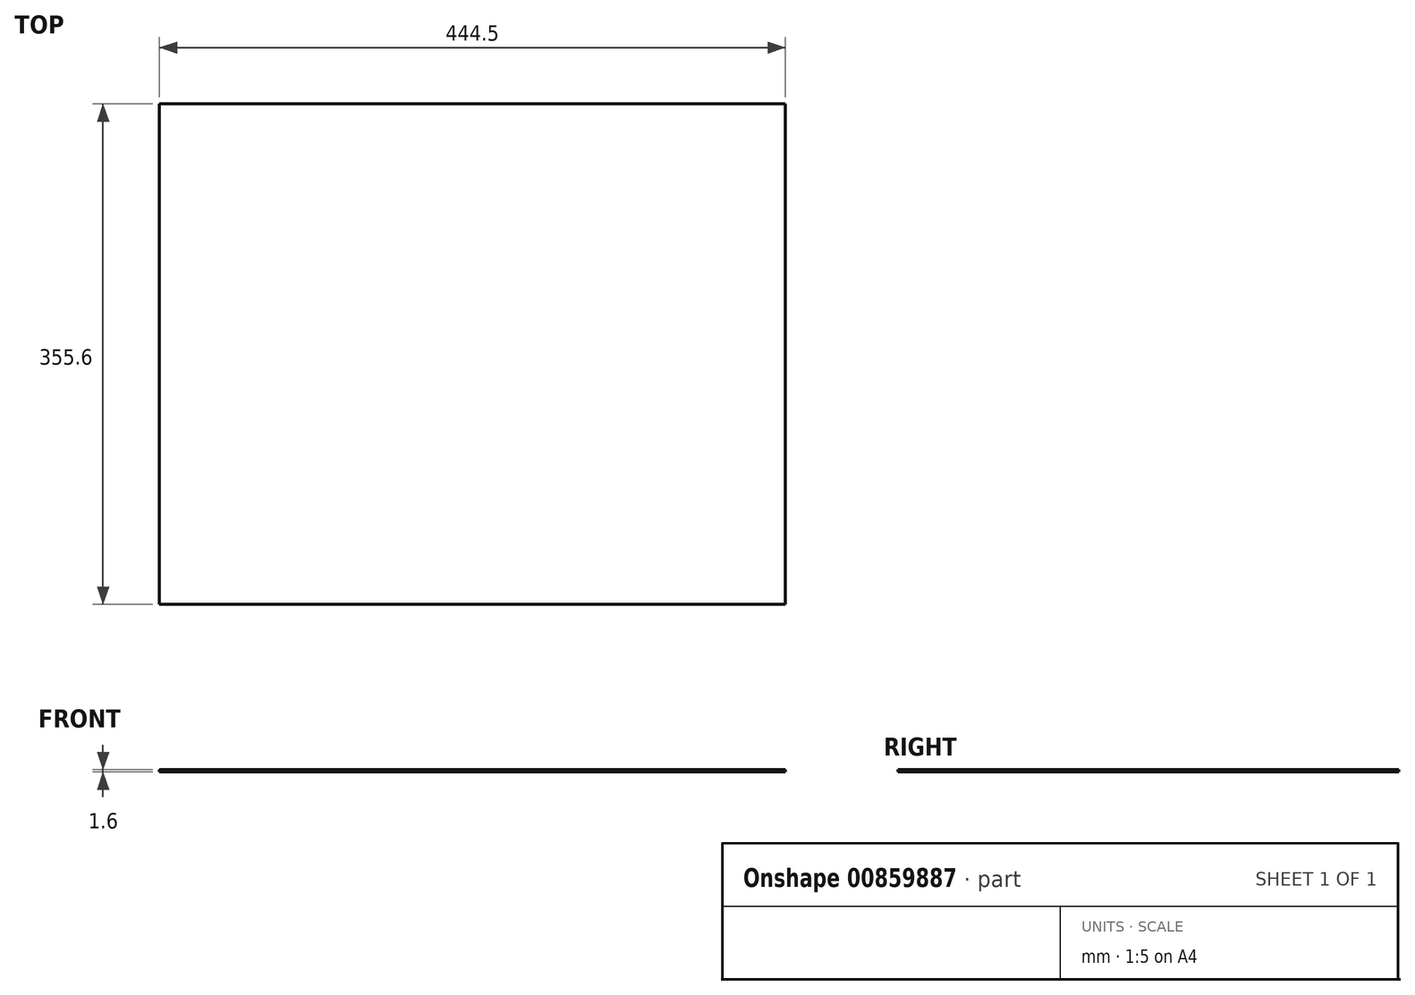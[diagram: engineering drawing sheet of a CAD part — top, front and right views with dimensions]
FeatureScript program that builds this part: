
annotation { "Feature Type Name" : "Feature", "Feature Type Description" : "" }
export const myFeature = defineFeature(function(context is Context, id is Id, definition is map)
    precondition{}
    {
        {
            assignVariable(context, id + "F0", {"name" : "ServerHeight", "anyValue" : 1.6});
        }
        {
            var Q0;
            Q0=qCreatedBy(makeId("Top.planeOp"),FACE);
            var sketch = newSketch(context, id + "F1", { "sketchPlane" : qUnion([Q0])});
            skLineSegment(sketch, "E0.bottom", {"start": v(222.25, -177.8) * mm, "end": v(-222.25, -177.8) * mm});
            skLineSegment(sketch, "E0.top", {"start": v(222.25, 177.8) * mm, "end": v(-222.25, 177.8) * mm});
            skLineSegment(sketch, "E0.left", {"start": v(222.25, -177.8) * mm, "end": v(222.25, 177.8) * mm});
            skLineSegment(sketch, "E0.right", {"start": v(-222.25, -177.8) * mm, "end": v(-222.25, 177.8) * mm});
            skPoint(sketch, "E0.middle", {"position": v(0, 0) * mm});
            skSolve(sketch);
        }
        {
            var Q0;
            Q0=makeQuery(id+"F1.imprint","IMPRINT",FACE,{"disambiguationData":[TD([[makeQuery(id+"F1.imprint","IMPRINT",EDGE,{"derivedFrom":sQuery(id+"F1.wireOp",EDGE,"E0.bottom")}),-1.0]])]});
            extrude(context, id + "F2", {"entities" : qUnion([Q0]), "depth" : (getVariable(context, 'ServerHeight')) * mm, "offsetDistance" : 25.4 * mm});
        }
        {
            var Q0;
            Q0=makeQuery(id+"F2.opExtrude","SWEPT_FACE",FACE,{"disambiguationData":[OSD([sQuery(id+"F1.wireOp",EDGE,"E0.left")])]});
            var sketch = newSketch(context, id + "F3", { "sketchPlane" : qUnion([Q0])});
            skLineSegment(sketch, "E1", {"start": v(0, 0) * mm, "end": v(177.8, 40.64) * mm, "construction": true});
            skPoint(sketch, "E2", {"position": v(88.9, 20.32) * mm});
            skSolve(sketch);
        }
    });
